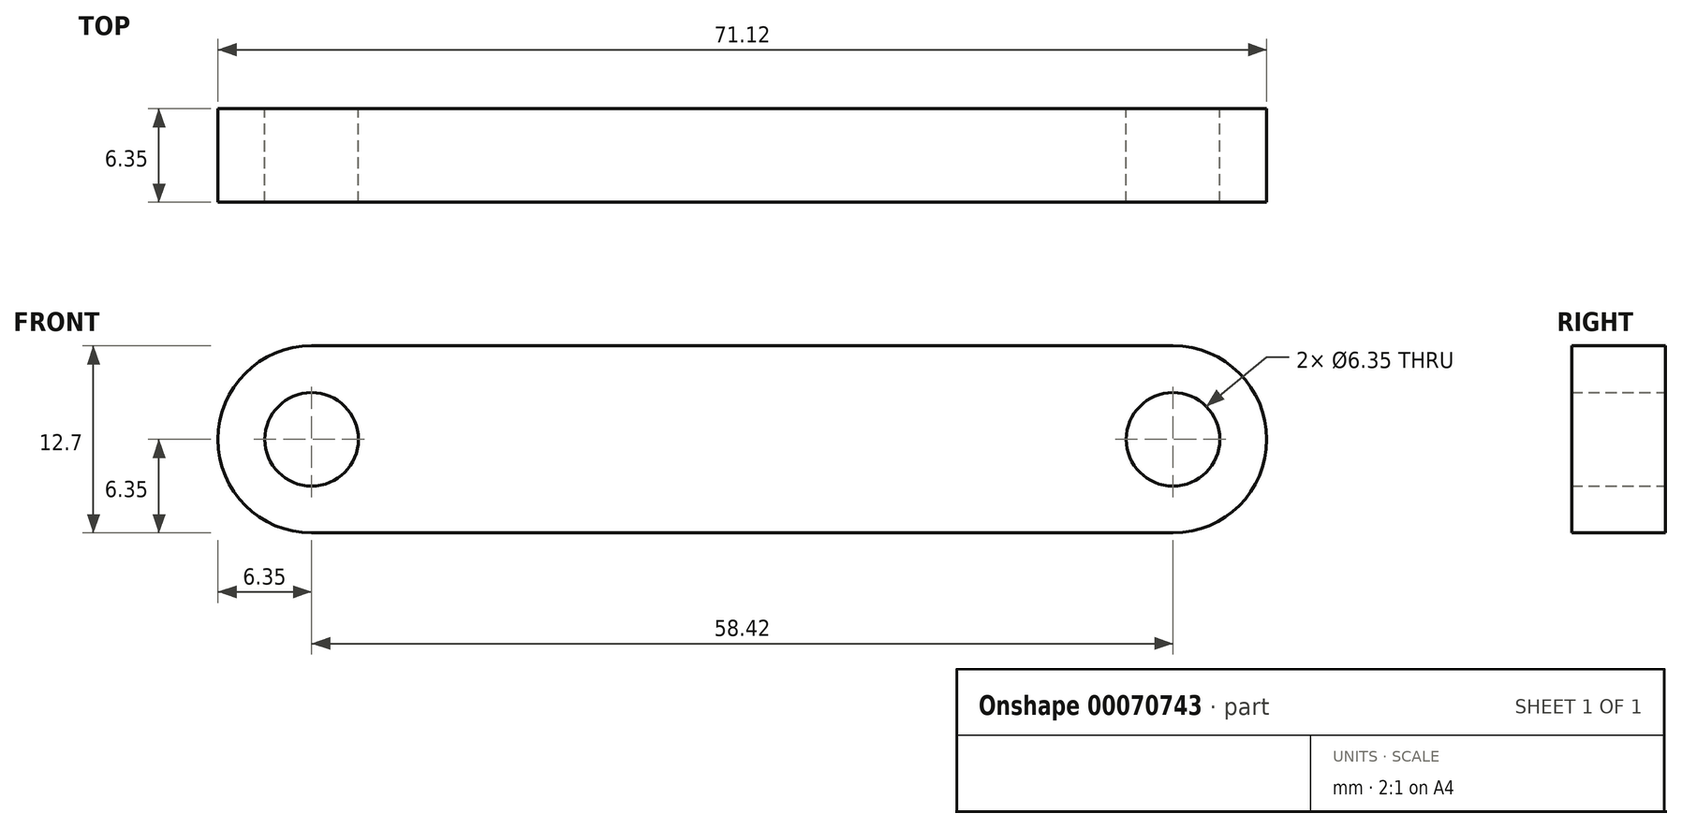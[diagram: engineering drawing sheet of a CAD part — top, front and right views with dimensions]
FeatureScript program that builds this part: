
annotation { "Feature Type Name" : "Feature", "Feature Type Description" : "" }
export const myFeature = defineFeature(function(context is Context, id is Id, definition is map)
    precondition{}
    {
        {
            var Q0;
            Q0=qCreatedBy(makeId("Front.planeOp"),FACE);
            var sketch = newSketch(context, id + "F0", { "sketchPlane" : qUnion([Q0])});
            skArc(sketch, "E0", {"start": v(0, 6.35) * mm, "mid": v(-6.35, 0) * mm, "end": v(0, -6.35) * mm});
            skLineSegment(sketch, "E1.bottom", {"start": v(0, 6.35) * mm, "end": v(58.42, 6.35) * mm});
            skLineSegment(sketch, "E1.top", {"start": v(0, -6.35) * mm, "end": v(58.42, -6.35) * mm});
            skArc(sketch, "E2", {"start": v(58.42, -6.35) * mm, "mid": v(64.77, 0) * mm, "end": v(58.42, 6.35) * mm});
            skCircle(sketch, "E3", {"center": v(0, 0) * mm, "radius": 3.18 * mm});
            skCircle(sketch, "E4", {"center": v(58.42, 0) * mm, "radius": 3.18 * mm});
            skSolve(sketch);
        }
        {
            var Q0;
            Q0=makeQuery(id+"F0.imprint","IMPRINT",FACE,{"disambiguationData":[TD([[makeQuery(id+"F0.imprint","IMPRINT",EDGE,{"derivedFrom":sQuery(id+"F0.wireOp",EDGE,"E0")}),1.0]])]});
            extrude(context, id + "F1", {"entities" : qUnion([Q0]), "depth" : 6.35 * mm});
        }
    });
